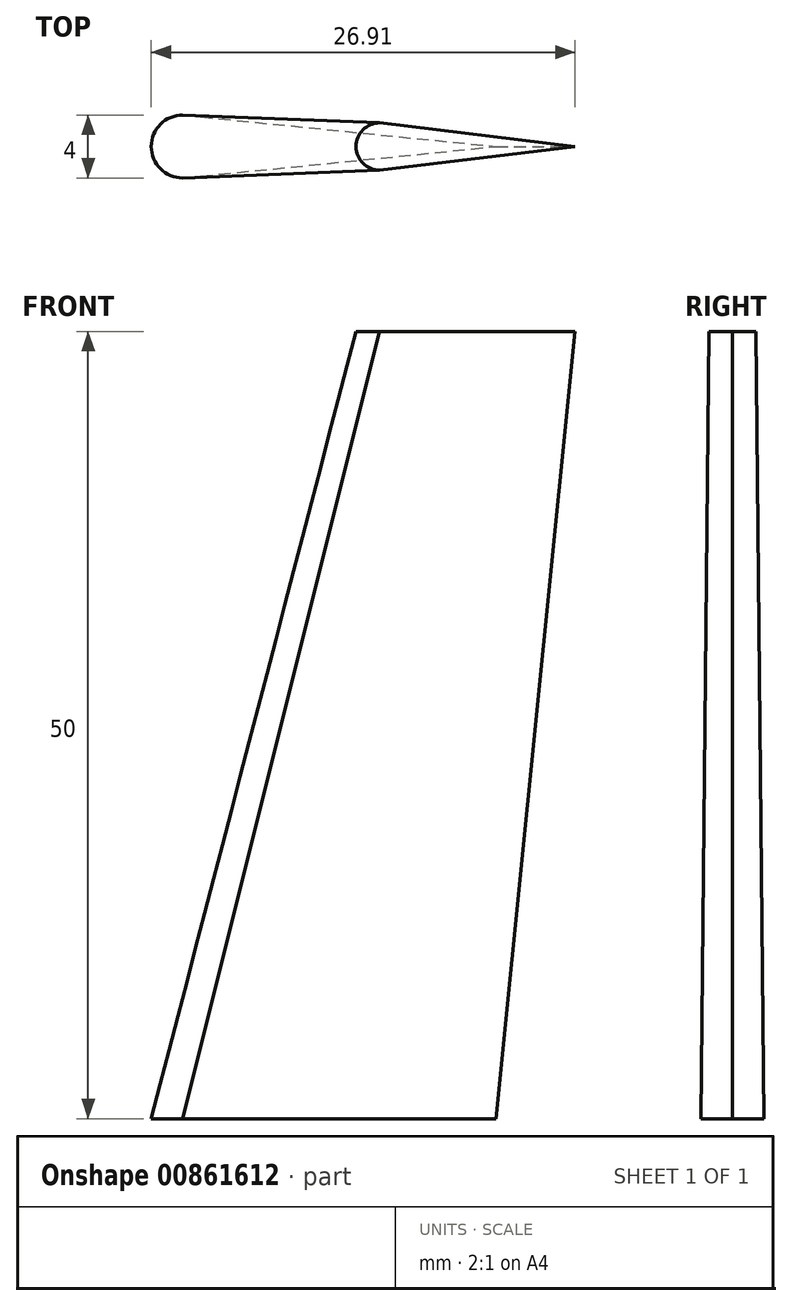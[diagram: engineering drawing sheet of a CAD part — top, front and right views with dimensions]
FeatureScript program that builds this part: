
annotation { "Feature Type Name" : "Feature", "Feature Type Description" : "" }
export const myFeature = defineFeature(function(context is Context, id is Id, definition is map)
    precondition{}
    {
        {
            var Q0;
            Q0=qCreatedBy(makeId("Top.planeOp"),FACE);
            var sketch = newSketch(context, id + "F0", { "sketchPlane" : qUnion([Q0])});
            skArc(sketch, "E0", {"start": v(0, 2) * mm, "mid": v(-2, 0) * mm, "end": v(0, -2) * mm});
            skLineSegment(sketch, "E1", {"start": v(0, -2) * mm, "end": v(19.9, 0) * mm});
            skLineSegment(sketch, "E2", {"start": v(0, 2) * mm, "end": v(19.9, 0) * mm});
            skSolve(sketch);
        }
        {
            var Q0;
            Q0=qCreatedBy(makeId("Top.planeOp"),FACE);
            cPlane(context, id + "F1", {"entities" : qUnion([Q0]), "cplaneType" : CPlaneType.OFFSET, "offset" : 50 * mm, "width" : 150 * mm, "height" : 150 * mm});
        }
        {
            var Q0;
            Q0=qCreatedBy(id+"F1.planeOp",FACE);
            var sketch = newSketch(context, id + "F2", { "sketchPlane" : qUnion([Q0])});
            skPoint(sketch, "E3", {"position": v(12.5, 0) * mm});
            skArc(sketch, "E4", {"start": v(12.5, 1.5) * mm, "mid": v(11, 0) * mm, "end": v(12.5, -1.5) * mm});
            skPoint(sketch, "E5", {"position": v(24.9, 0) * mm});
            skLineSegment(sketch, "E6", {"start": v(12.5, 1.5) * mm, "end": v(24.9, 0) * mm});
            skLineSegment(sketch, "E7", {"start": v(24.9, 0) * mm, "end": v(12.5, -1.5) * mm});
            skSolve(sketch);
        }
        {
            var Q0;
            Q0=makeQuery(id+"F0.imprint","IMPRINT",FACE,{"disambiguationData":[TD([[makeQuery(id+"F0.imprint","IMPRINT",EDGE,{"derivedFrom":sQuery(id+"F0.wireOp",EDGE,"E0")}),1.0]])]});
            var Q1;
            Q1=makeQuery(id+"F2.imprint","IMPRINT",FACE,{"disambiguationData":[TD([[makeQuery(id+"F2.imprint","IMPRINT",EDGE,{"derivedFrom":sQuery(id+"F2.wireOp",EDGE,"E4")}),1.0]])]});
            loft(context, id + "F3", {"sheetProfilesArray" : [{ "sheetProfileEntities" : qUnion([Q0]) }, { "sheetProfileEntities" : qUnion([Q1]) }]});
        }
    });
